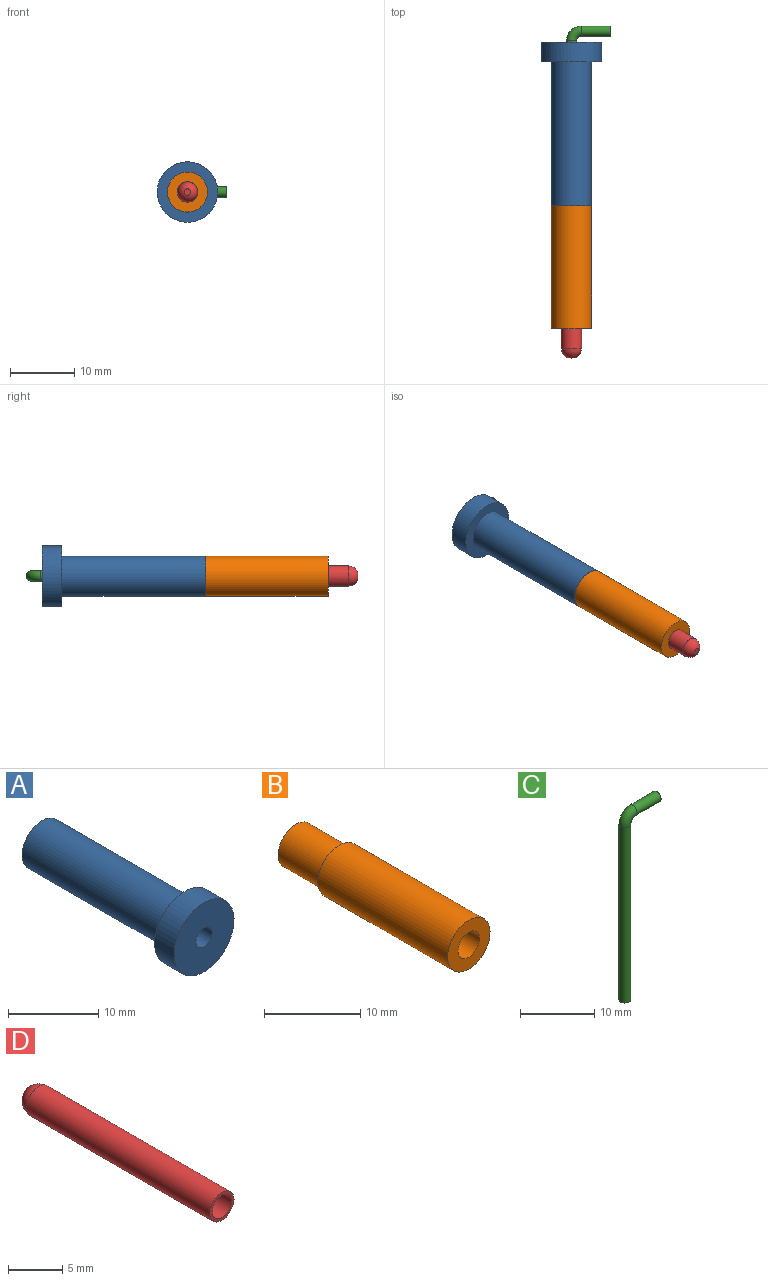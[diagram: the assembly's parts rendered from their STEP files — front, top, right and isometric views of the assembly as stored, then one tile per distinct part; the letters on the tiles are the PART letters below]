
ASSEMBLY  parts=4 mates=3
PART A: 8 faces, bbox 9.4x25.4x9.4 mm
  f0: cylinder r=3.11mm len=22.35mm, axis (0,1,0), area 437mm2, adj f3,f7
  f1: cylinder r=1.27mm len=19.02mm, axis (0,-1,0), area 151.8mm2, adj f2,f4
  f2: plane 9.39x9.39mm, normal (0,-1,0), area 64.2mm2, adj f1,f6
  f3: plane 6.22x6.22mm, normal (0,1,0), area 8.9mm2, adj f0,f5
  f4: plane 5.23x5.23mm, normal (0,1,0), area 16.4mm2, adj f1,f5
  f5: cylinder r=2.62mm len=6.38mm, axis (0,1,0), area 104.8mm2, adj f3,f4
  f6: cylinder r=4.7mm len=9.39mm, axis (0,-1,0), area 89.9mm2, adj f2,f7
  f7: plane 9.39x9.39mm, normal (0,1,0), area 38.9mm2, adj f0,f6
PART B: 8 faces, bbox 6.2x25.4x6.2 mm
  f0: cylinder r=3.11mm len=19.05mm, axis (0,1,0), area 372.4mm2, adj f3,f7
  f1: plane 5.21x5.21mm, normal (0,1,0), area 6.7mm2, adj f4,f6
  f2: cylinder r=1.59mm len=3.18mm, axis (0,1,0), area 25.3mm2, adj f3,f5
  f3: plane 6.22x6.22mm, normal (0,-1,0), area 22.5mm2, adj f0,f2
  f4: cylinder r=2.16mm len=22.86mm, axis (0,1,0), area 310.1mm2, adj f1,f5
  f5: plane 4.32x4.32mm, normal (0,1,0), area 6.7mm2, adj f2,f4
  f6: cylinder r=2.6mm len=6.35mm, axis (0,1,0), area 103.9mm2, adj f1,f7
  f7: plane 6.22x6.22mm, normal (0,1,0), area 9.1mm2, adj f0,f6
PART C: 5 faces, bbox 7.1x1.6x31.5 mm
  f0: plane 1.59x1.59mm, normal (0,0,-1), area 2mm2, adj f2
  f1: plane 1.59x1.59mm, normal (1,0,0), area 2mm2, adj f4
  f2: cylinder r=0.79mm len=28.96mm, axis (0,0,1), area 144.4mm2, adj f0,f3
  f3: torus R=1.52mm, axis (0,1,0), area 11.9mm2, adj f2,f4
  f4: cylinder r=0.79mm len=4.57mm, axis (1,0,0), area 22.8mm2, adj f1,f3
PART D: 7 faces, bbox 3.2x25.4x3.2 mm
  f0: cylinder r=1.59mm len=23.97mm, axis (0,1,0), area 239mm2, adj f1,f2
  f1: plane 3.18x3.18mm, normal (0,-1,0), area 2.9mm2, adj f0,f5
  f2: cone r=1.55mm half-angle=52deg, axis (0,1,0), area 0.5mm2, adj f0,f3
  f3: sphere r=1.55mm, area 14.3mm2, adj f2,f4
  f4: plane 1.01x1.01mm, normal (0,1,0), area 0.8mm2, adj f3
  f5: cylinder r=1.27mm len=5.08mm, axis (0,-1,0), area 40.5mm2, adj f1,f6
  f6: plane 2.54x2.54mm, normal (0,-1,0), area 5.1mm2, adj f5
PLACE A rot(axis=(1,0,0),180deg) t=(-7.29,-7.79,-4.03)mm
PLACE B rot(axis=(-0.09,0.38,-0.92),0deg) t=(-7.29,-1.43,-4.03)mm
PLACE C rot(axis=(-1,0,0),90deg) t=(-7.29,-11.15,-4.03)mm
PLACE D rot(axis=(1,0,0),180deg) t=(-7.29,-31.47,-4.03)mm
MATE fastened D.f5 <-> C.f2  axis (0,1,0) through (-7.29,-11.15,-4.03)mm
MATE cylindrical C.f2 <-> B.f0  axis (0,-1,0) through (-7.29,-11.15,-4.03)mm
MATE slider A.f1 <-> B.f4  axis (0,-1,0) through (-7.29,-1.41,-4.03)mm
